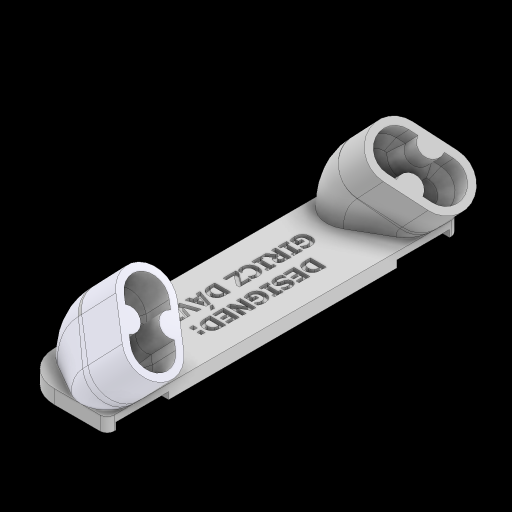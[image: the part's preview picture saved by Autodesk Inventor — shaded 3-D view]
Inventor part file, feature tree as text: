
AUTODESK INVENTOR PART (.ipt)
format: ipt  version: 2023 (Build 270158000, 158)  size: 896,000 bytes
history: native  units: mm
features: extrude x16, sketch x11, plane x2, revolve x2, chamfer x2, fillet x2, sweep x1, mirror x1
ambient origin geometry x8: Origin, YZ Plane, XZ Plane, XY Plane, X Axis, Y Axis, Z Axis, Center Point
bodies: Solid1 (feature_tree)
feature tree (37):
  sketch  "Sketch1"  dims[d0=100.0mm d1=25.0mm d2=7.5mm d3=7.5mm d4=60.0deg d5=15.0mm d6=11.0mm d7=11.0mm d8=15.0mm d11=135.0deg]
  plane  "Work Plane1"
  sweep  "Sweep1"
  extrude  "Extrusion1"  Depth=4.0mm TaperAngle=0.0deg
  revolve  "Revolution1"  Angle=45.0deg
  sketch  "Sketch6"  dims[d31=10.0mm d32=45.0deg]
  extrude  "Extrusion4"  TaperAngle=45.0deg  [1 undecoded]
  extrude  "Extrusion5"  Depth=10.0mm
  sketch  "Sketch7"  dims[d33=10.0mm d34=10.0mm]
  extrude  "Extrusion6"  Depth=10.0mm
  extrude  "Extrusion7"  Depth=15.0mm
  mirror  "Mirror4"
  plane  "Work Plane9"
  extrude  "Extrusion8"  Depth=5.5mm
  revolve  "Revolution2"  [1 undecoded]
  extrude  "Extrusion9"  Depth=6.5mm
  sketch  "Sketch19"  dims[d60=5.5mm d61=5.5mm]
  extrude  "Extrusion10"  Depth=12.5mm TaperAngle=0.0deg
  extrude  "Extrusion11"  Depth=325.0mm TaperAngle=0.0deg
  extrude  "Extrusion12"  Depth=7.5mm
  sketch  "Sketch21"  dims[d65=2.0mm d66=6.5mm]
  extrude  "Extrusion13"  TaperAngle=90.0deg  [1 undecoded]
  chamfer  "Chamfer3"  Distance=7.5mm
  chamfer  "Chamfer4"  Distance=5.5mm
  extrude  "Extrusion15"  Depth=5.5mm
  extrude  "Extrusion18"  Depth=15.0mm
  fillet  "Fillet2"  Radius=11.0mm
  fillet  "Fillet3"  Radius=11.0mm
  extrude  "Extrusion19"  Depth=2.0mm
  extrude  "Extrusion20"  Depth=6.5mm
  extrude  "Extrusion21"  Depth=6.5mm
  sketch  "Sketch3"  dims[d12=0.0mm d13=0.0mm d14=4.0mm d15=0.0mm]
  sketch  "Sketch5"  dims[d29=11.389087mm d30=45.0deg]
  sketch  "Sketch14"  dims[d35=45.0deg d37=10.0mm]
  sketch  "Sketch15"  dims[d38=0.977384mm d57=15.0mm]
  sketch  "Sketch20"  dims[d63=11.0mm d64=11.0mm]
  sketch  "Sketch22"  dims[d67=6.5mm d68=12.5mm d69=0.0mm d70=325.0mm d71=0.0mm d72=7.5mm d73=90.0deg d74=7.5mm d75=5.5mm d76=5.5mm d77=15.0mm d78=11.0mm d79=11.0mm d80=2.0mm d81=6.5mm d82=6.5mm d83=10.0mm d84=0.0mm d93=10.0mm d94=0.0mm d115=20.0mm d116=0.0mm d131=8.726646mm d132=300.0mm d133=0.0mm d134=15.0mm d135=300.0mm d136=0.0mm d137=11.0mm d138=11.0mm d139=2.0mm d140=6.5mm d141=6.5mm d142=10.0mm d143=0.0mm d144=40.0mm d145=0.0mm d146=25.0mm d147=100.0mm d150=15.0mm d151=5.5mm d152=2.0mm d153=0.0mm d156=2.0mm d157=4.0mm d158=45.0deg d159=2.0mm d160=4.0mm d161=45.0deg d162=549.891mm d163=50.0mm d164=100.0mm d167=2.5mm d169=15.0mm d170=17.5mm d171=17.5mm d174=10.0mm d175=300.0mm d176=0.0mm d177=7.5mm d183=2.0mm d184=0.0mm d185=2.0mm d186=10.0mm d187=3.0mm d188=0.0mm d189=15.0mm d190=0.0mm d191=1.0mm d192=0.0mm d178=0.872665mm]
note: 3 required parameter values undecoded (feature->parameter linkage not recoverable at this tier; creation-order binding heuristic only, values carry confidence <= 0.55)